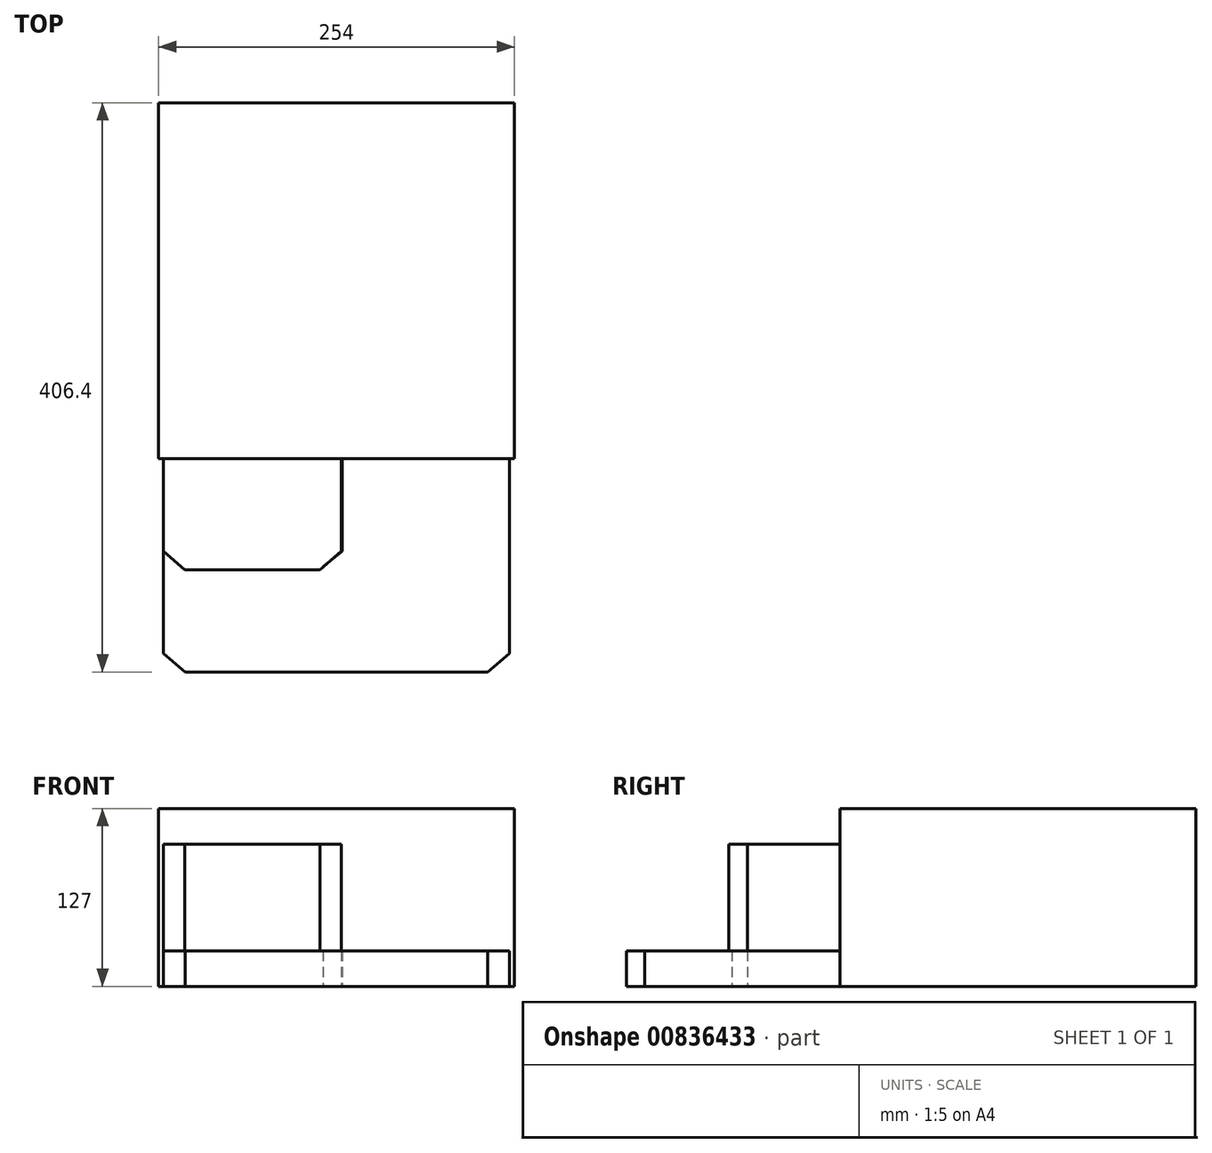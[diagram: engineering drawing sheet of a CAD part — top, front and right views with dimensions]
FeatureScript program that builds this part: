
annotation { "Feature Type Name" : "Feature", "Feature Type Description" : "" }
export const myFeature = defineFeature(function(context is Context, id is Id, definition is map)
    precondition{}
    {
        {
            var Q0;
            Q0=qCreatedBy(makeId("Top.planeOp"),FACE);
            var sketch = newSketch(context, id + "F0", { "sketchPlane" : qUnion([Q0])});
            skLineSegment(sketch, "E0.bottom", {"start": v(-131.57, 277.89) * mm, "end": v(122.43, 277.89) * mm});
            skLineSegment(sketch, "E0.top", {"start": v(-131.57, 23.89) * mm, "end": v(122.43, 23.89) * mm});
            skLineSegment(sketch, "E0.left", {"start": v(-131.57, 277.89) * mm, "end": v(-131.57, 23.89) * mm});
            skLineSegment(sketch, "E0.right", {"start": v(122.43, 277.89) * mm, "end": v(122.43, 23.89) * mm});
            skSolve(sketch);
        }
        {
            var Q0;
            Q0=makeQuery(id+"F0.imprint","IMPRINT",FACE,{"disambiguationData":[TD([[makeQuery(id+"F0.imprint","IMPRINT",EDGE,{"derivedFrom":sQuery(id+"F0.wireOp",EDGE,"E0.bottom")}),-1.0]])]});
            var sketch = newSketch(context, id + "F1", { "sketchPlane" : qUnion([Q0])});
            skLineSegment(sketch, "E1.bottom", {"start": v(-128.27, 23.89) * mm, "end": v(-1.27, 23.89) * mm});
            skLineSegment(sketch, "E1.left", {"start": v(-128.27, 23.89) * mm, "end": v(-128.27, -42.15) * mm});
            skLineSegment(sketch, "E1.right", {"start": v(-1.27, 23.89) * mm, "end": v(-1.27, -42.15) * mm});
            skLineSegment(sketch, "E2", {"start": v(-128.27, -42.15) * mm, "end": v(-113.03, -55.6) * mm});
            skLineSegment(sketch, "E3", {"start": v(-113.03, -55.6) * mm, "end": v(-16.5, -55.6) * mm});
            skLineSegment(sketch, "E4", {"start": v(-16.5, -55.6) * mm, "end": v(-1.27, -42.15) * mm});
            skSolve(sketch);
        }
        {
            var Q0;
            Q0 = qSketchRegion(id + "F0", true);
            extrude(context, id + "F2", {"entities" : qUnion([Q0]), "depth" : 127 * mm, "offsetDistance" : 25.4 * mm});
        }
        {
            var Q0;
            Q0=makeQuery(id+"F1.imprint","IMPRINT",FACE,{"disambiguationData":[TD([[makeQuery(id+"F1.imprint","IMPRINT",EDGE,{"derivedFrom":sQuery(id+"F1.wireOp",EDGE,"E1.bottom")}),-1.0]])]});
            extrude(context, id + "F3", {"entities" : qUnion([Q0]), "operationType" : NewBodyOperationType.ADD, "depth" : 101.6 * mm, "offsetDistance" : 25.4 * mm});
        }
        {
            var Q0;
            Q0=qCreatedBy(makeId("Top.planeOp"),FACE);
            var sketch = newSketch(context, id + "F4", { "sketchPlane" : qUnion([Q0])});
            skLineSegment(sketch, "E5", {"start": v(118.75, -115.44) * mm, "end": v(103.2, -128.51) * mm});
            skLineSegment(sketch, "E6", {"start": v(103.2, -128.51) * mm, "end": v(-112.7, -128.51) * mm});
            skLineSegment(sketch, "E7", {"start": v(-112.7, -128.51) * mm, "end": v(-128.27, -115.44) * mm});
            skLineSegment(sketch, "E8", {"start": v(-128.27, -115.44) * mm, "end": v(-128.27, -42.15) * mm});
            skLineSegment(sketch, "E9", {"start": v(-128.27, -42.15) * mm, "end": v(-112.7, -55.22) * mm});
            skLineSegment(sketch, "E10", {"start": v(-112.7, -55.22) * mm, "end": v(-16.19, -55.22) * mm});
            skLineSegment(sketch, "E11", {"start": v(-16.19, -55.22) * mm, "end": v(-0.63, -42.15) * mm});
            skLineSegment(sketch, "E12", {"start": v(-0.63, -42.15) * mm, "end": v(-0.63, 23.89) * mm});
            skLineSegment(sketch, "E13", {"start": v(-0.63, 23.89) * mm, "end": v(118.75, 23.89) * mm});
            skLineSegment(sketch, "E14", {"start": v(118.75, 23.89) * mm, "end": v(118.75, -115.44) * mm});
            skSolve(sketch);
        }
        {
            var Q0;
            Q0 = qSketchRegion(id + "F4", true);
            extrude(context, id + "F5", {"entities" : qUnion([Q0]), "operationType" : NewBodyOperationType.ADD, "depth" : 25.4 * mm, "offsetDistance" : 25.4 * mm});
        }
    });
